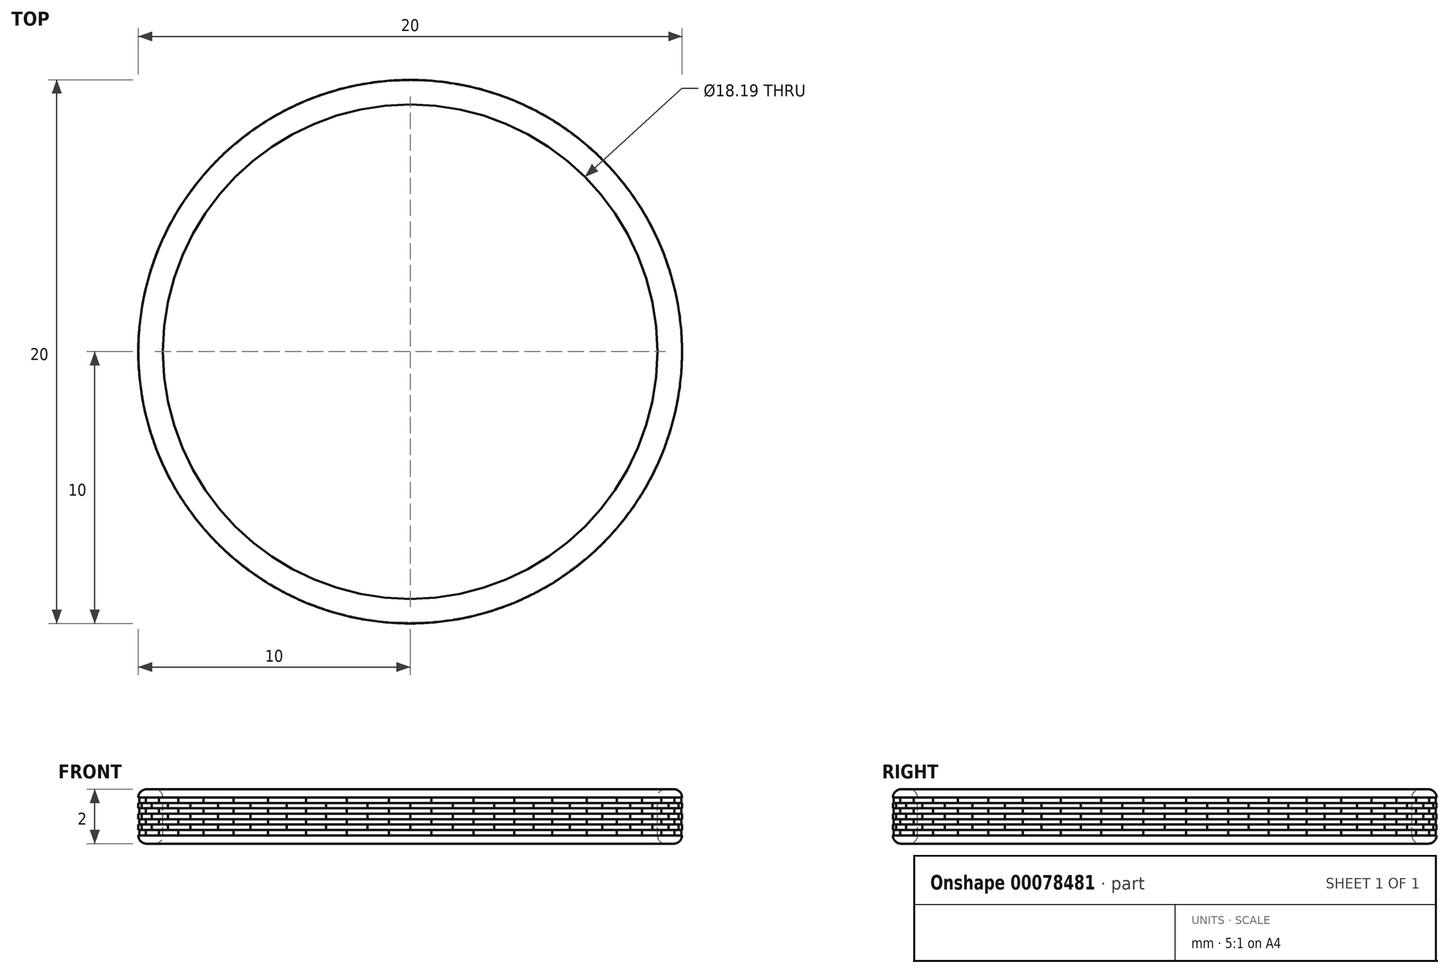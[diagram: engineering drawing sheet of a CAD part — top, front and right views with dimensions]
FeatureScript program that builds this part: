
annotation { "Feature Type Name" : "Feature", "Feature Type Description" : "" }
export const myFeature = defineFeature(function(context is Context, id is Id, definition is map)
    precondition{}
    {
        {
            var Q0;
            Q0=qCreatedBy(makeId("Top.planeOp"),FACE);
            var sketch = newSketch(context, id + "F0", { "sketchPlane" : qUnion([Q0])});
            skCircle(sketch, "E0", {"center": v(0, 0) * mm, "radius": 9.1 * mm});
            skLineSegment(sketch, "E1", {"start": v(0, 0) * mm, "end": v(-9.1, 0) * mm, "construction": true});
            skSolve(sketch);
        }
        {
            var Q0;
            Q0=qCreatedBy(makeId("Top.planeOp"),FACE);
            var sketch = newSketch(context, id + "F1", { "sketchPlane" : qUnion([Q0])});
            skCircle(sketch, "E2.cCircle", {"center": v(0, 0) * mm, "radius": 10 * mm, "construction": true});
            skLineSegment(sketch, "E2.0", {"start": v(10, 0) * mm, "end": v(9.88, -1.56) * mm});
            skLineSegment(sketch, "E2.1", {"start": v(9.88, -1.56) * mm, "end": v(9.51, -3.1) * mm});
            skLineSegment(sketch, "E2.2", {"start": v(9.51, -3.1) * mm, "end": v(8.91, -4.54) * mm});
            skLineSegment(sketch, "E2.3", {"start": v(8.91, -4.54) * mm, "end": v(8.1, -5.88) * mm});
            skLineSegment(sketch, "E2.4", {"start": v(8.1, -5.88) * mm, "end": v(7.07, -7.07) * mm});
            skLineSegment(sketch, "E2.5", {"start": v(7.07, -7.07) * mm, "end": v(5.88, -8.1) * mm});
            skLineSegment(sketch, "E2.6", {"start": v(5.88, -8.1) * mm, "end": v(4.54, -8.91) * mm});
            skLineSegment(sketch, "E2.7", {"start": v(4.54, -8.91) * mm, "end": v(3.1, -9.51) * mm});
            skLineSegment(sketch, "E2.8", {"start": v(3.1, -9.51) * mm, "end": v(1.56, -9.88) * mm});
            skLineSegment(sketch, "E2.9", {"start": v(1.56, -9.88) * mm, "end": v(0, -10) * mm});
            skLineSegment(sketch, "E2.10", {"start": v(0, -10) * mm, "end": v(-1.56, -9.88) * mm});
            skLineSegment(sketch, "E2.11", {"start": v(-1.56, -9.88) * mm, "end": v(-3.1, -9.51) * mm});
            skLineSegment(sketch, "E2.12", {"start": v(-3.1, -9.51) * mm, "end": v(-4.54, -8.91) * mm});
            skLineSegment(sketch, "E2.13", {"start": v(-4.54, -8.91) * mm, "end": v(-5.88, -8.1) * mm});
            skLineSegment(sketch, "E2.14", {"start": v(-5.88, -8.1) * mm, "end": v(-7.07, -7.07) * mm});
            skLineSegment(sketch, "E2.15", {"start": v(-7.07, -7.07) * mm, "end": v(-8.1, -5.88) * mm});
            skLineSegment(sketch, "E2.16", {"start": v(-8.1, -5.88) * mm, "end": v(-8.91, -4.54) * mm});
            skLineSegment(sketch, "E2.17", {"start": v(-8.91, -4.54) * mm, "end": v(-9.51, -3.1) * mm});
            skLineSegment(sketch, "E2.18", {"start": v(-9.51, -3.1) * mm, "end": v(-9.88, -1.56) * mm});
            skLineSegment(sketch, "E2.19", {"start": v(-9.88, -1.56) * mm, "end": v(-10, 0) * mm});
            skLineSegment(sketch, "E2.20", {"start": v(-10, 0) * mm, "end": v(-9.88, 1.56) * mm});
            skLineSegment(sketch, "E2.21", {"start": v(-9.88, 1.56) * mm, "end": v(-9.51, 3.1) * mm});
            skLineSegment(sketch, "E2.22", {"start": v(-9.51, 3.1) * mm, "end": v(-8.91, 4.54) * mm});
            skLineSegment(sketch, "E2.23", {"start": v(-8.91, 4.54) * mm, "end": v(-8.1, 5.88) * mm});
            skLineSegment(sketch, "E2.24", {"start": v(-8.1, 5.88) * mm, "end": v(-7.07, 7.07) * mm});
            skLineSegment(sketch, "E2.25", {"start": v(-7.07, 7.07) * mm, "end": v(-5.88, 8.1) * mm});
            skLineSegment(sketch, "E2.26", {"start": v(-5.88, 8.1) * mm, "end": v(-4.54, 8.91) * mm});
            skLineSegment(sketch, "E2.27", {"start": v(-4.54, 8.91) * mm, "end": v(-3.1, 9.51) * mm});
            skLineSegment(sketch, "E2.28", {"start": v(-3.1, 9.51) * mm, "end": v(-1.56, 9.88) * mm});
            skLineSegment(sketch, "E2.29", {"start": v(-1.56, 9.88) * mm, "end": v(0, 10) * mm});
            skLineSegment(sketch, "E2.30", {"start": v(0, 10) * mm, "end": v(1.56, 9.88) * mm});
            skLineSegment(sketch, "E2.31", {"start": v(1.56, 9.88) * mm, "end": v(3.1, 9.51) * mm});
            skLineSegment(sketch, "E2.32", {"start": v(3.1, 9.51) * mm, "end": v(4.54, 8.91) * mm});
            skLineSegment(sketch, "E2.33", {"start": v(4.54, 8.91) * mm, "end": v(5.88, 8.1) * mm});
            skLineSegment(sketch, "E2.34", {"start": v(5.88, 8.1) * mm, "end": v(7.07, 7.07) * mm});
            skLineSegment(sketch, "E2.35", {"start": v(7.07, 7.07) * mm, "end": v(8.1, 5.88) * mm});
            skLineSegment(sketch, "E2.36", {"start": v(8.1, 5.88) * mm, "end": v(8.91, 4.54) * mm});
            skLineSegment(sketch, "E2.37", {"start": v(8.91, 4.54) * mm, "end": v(9.51, 3.1) * mm});
            skLineSegment(sketch, "E2.38", {"start": v(9.51, 3.1) * mm, "end": v(9.88, 1.56) * mm});
            skLineSegment(sketch, "E2.39", {"start": v(9.88, 1.56) * mm, "end": v(10, 0) * mm});
            skLineSegment(sketch, "E3", {"start": v(0, 0) * mm, "end": v(-10, 0) * mm});
            skSolve(sketch);
        }
        {
            var Q0;
            Q0 = qSketchRegion(id + "F1", true);
            extrude(context, id + "F2", {"entities" : qUnion([Q0]), "endBound" : BoundingType.SYMMETRIC, "depth" : .2 * mm});
        }
        {
            var Q0;
            Q0=makeQuery(id+"F2.opExtrude","CAP_FACE",FACE,{"disambiguationData":[OSD([sQuery(id+"F1.wireOp",EDGE,"E2.0"),sQuery(id+"F1.wireOp",EDGE,"E2.1"),sQuery(id+"F1.wireOp",EDGE,"E2.2"),sQuery(id+"F1.wireOp",EDGE,"E2.3"),sQuery(id+"F1.wireOp",EDGE,"E2.4"),sQuery(id+"F1.wireOp",EDGE,"E2.5"),sQuery(id+"F1.wireOp",EDGE,"E2.6"),sQuery(id+"F1.wireOp",EDGE,"E2.7"),sQuery(id+"F1.wireOp",EDGE,"E2.8"),sQuery(id+"F1.wireOp",EDGE,"E2.9"),sQuery(id+"F1.wireOp",EDGE,"E2.10"),sQuery(id+"F1.wireOp",EDGE,"E2.11"),sQuery(id+"F1.wireOp",EDGE,"E2.12"),sQuery(id+"F1.wireOp",EDGE,"E2.13"),sQuery(id+"F1.wireOp",EDGE,"E2.14"),sQuery(id+"F1.wireOp",EDGE,"E2.15"),sQuery(id+"F1.wireOp",EDGE,"E2.16"),sQuery(id+"F1.wireOp",EDGE,"E2.17"),sQuery(id+"F1.wireOp",EDGE,"E2.18"),sQuery(id+"F1.wireOp",EDGE,"E2.19"),sQuery(id+"F1.wireOp",EDGE,"E2.20"),sQuery(id+"F1.wireOp",EDGE,"E2.21"),sQuery(id+"F1.wireOp",EDGE,"E2.22"),sQuery(id+"F1.wireOp",EDGE,"E2.23"),sQuery(id+"F1.wireOp",EDGE,"E2.24"),sQuery(id+"F1.wireOp",EDGE,"E2.25"),sQuery(id+"F1.wireOp",EDGE,"E2.26"),sQuery(id+"F1.wireOp",EDGE,"E2.27"),sQuery(id+"F1.wireOp",EDGE,"E2.28"),sQuery(id+"F1.wireOp",EDGE,"E2.29"),sQuery(id+"F1.wireOp",EDGE,"E2.30"),sQuery(id+"F1.wireOp",EDGE,"E2.31"),sQuery(id+"F1.wireOp",EDGE,"E2.32"),sQuery(id+"F1.wireOp",EDGE,"E2.33"),sQuery(id+"F1.wireOp",EDGE,"E2.34"),sQuery(id+"F1.wireOp",EDGE,"E2.35"),sQuery(id+"F1.wireOp",EDGE,"E2.36"),sQuery(id+"F1.wireOp",EDGE,"E2.37"),sQuery(id+"F1.wireOp",EDGE,"E2.38"),sQuery(id+"F1.wireOp",EDGE,"E2.39")])],"isStart":false});
            var sketch = newSketch(context, id + "F3", { "sketchPlane" : qUnion([Q0])});
            skCircle(sketch, "E4.cCircle", {"center": v(0, 0) * mm, "radius": 10 * mm, "construction": true});
            skLineSegment(sketch, "E4.0", {"start": v(9.24, 3.83) * mm, "end": v(9.72, 2.33) * mm});
            skLineSegment(sketch, "E4.1", {"start": v(9.72, 2.33) * mm, "end": v(9.97, 0.78) * mm});
            skLineSegment(sketch, "E4.2", {"start": v(9.97, 0.78) * mm, "end": v(9.97, -0.78) * mm});
            skLineSegment(sketch, "E4.3", {"start": v(9.97, -0.78) * mm, "end": v(9.72, -2.33) * mm});
            skLineSegment(sketch, "E4.4", {"start": v(9.72, -2.33) * mm, "end": v(9.24, -3.83) * mm});
            skLineSegment(sketch, "E4.5", {"start": v(9.24, -3.83) * mm, "end": v(8.53, -5.22) * mm});
            skLineSegment(sketch, "E4.6", {"start": v(8.53, -5.22) * mm, "end": v(7.6, -6.5) * mm});
            skLineSegment(sketch, "E4.7", {"start": v(7.6, -6.5) * mm, "end": v(6.5, -7.6) * mm});
            skLineSegment(sketch, "E4.8", {"start": v(6.5, -7.6) * mm, "end": v(5.22, -8.53) * mm});
            skLineSegment(sketch, "E4.9", {"start": v(5.22, -8.53) * mm, "end": v(3.83, -9.24) * mm});
            skLineSegment(sketch, "E4.10", {"start": v(3.83, -9.24) * mm, "end": v(2.33, -9.72) * mm});
            skLineSegment(sketch, "E4.11", {"start": v(2.33, -9.72) * mm, "end": v(0.78, -9.97) * mm});
            skLineSegment(sketch, "E4.12", {"start": v(0.78, -9.97) * mm, "end": v(-0.78, -9.97) * mm});
            skLineSegment(sketch, "E4.13", {"start": v(-0.78, -9.97) * mm, "end": v(-2.33, -9.72) * mm});
            skLineSegment(sketch, "E4.14", {"start": v(-2.33, -9.72) * mm, "end": v(-3.83, -9.24) * mm});
            skLineSegment(sketch, "E4.15", {"start": v(-3.83, -9.24) * mm, "end": v(-5.22, -8.53) * mm});
            skLineSegment(sketch, "E4.16", {"start": v(-5.22, -8.53) * mm, "end": v(-6.5, -7.6) * mm});
            skLineSegment(sketch, "E4.17", {"start": v(-6.5, -7.6) * mm, "end": v(-7.6, -6.5) * mm});
            skLineSegment(sketch, "E4.18", {"start": v(-7.6, -6.5) * mm, "end": v(-8.53, -5.22) * mm});
            skLineSegment(sketch, "E4.19", {"start": v(-8.53, -5.22) * mm, "end": v(-9.24, -3.83) * mm});
            skLineSegment(sketch, "E4.20", {"start": v(-9.24, -3.83) * mm, "end": v(-9.72, -2.33) * mm});
            skLineSegment(sketch, "E4.21", {"start": v(-9.72, -2.33) * mm, "end": v(-9.97, -0.78) * mm});
            skLineSegment(sketch, "E4.22", {"start": v(-9.97, -0.78) * mm, "end": v(-9.97, 0.78) * mm});
            skLineSegment(sketch, "E4.23", {"start": v(-9.97, 0.78) * mm, "end": v(-9.72, 2.33) * mm});
            skLineSegment(sketch, "E4.24", {"start": v(-9.72, 2.33) * mm, "end": v(-9.24, 3.83) * mm});
            skLineSegment(sketch, "E4.25", {"start": v(-9.24, 3.83) * mm, "end": v(-8.53, 5.22) * mm});
            skLineSegment(sketch, "E4.26", {"start": v(-8.53, 5.22) * mm, "end": v(-7.6, 6.5) * mm});
            skLineSegment(sketch, "E4.27", {"start": v(-7.6, 6.5) * mm, "end": v(-6.5, 7.6) * mm});
            skLineSegment(sketch, "E4.28", {"start": v(-6.5, 7.6) * mm, "end": v(-5.22, 8.53) * mm});
            skLineSegment(sketch, "E4.29", {"start": v(-5.22, 8.53) * mm, "end": v(-3.83, 9.24) * mm});
            skLineSegment(sketch, "E4.30", {"start": v(-3.83, 9.24) * mm, "end": v(-2.33, 9.72) * mm});
            skLineSegment(sketch, "E4.31", {"start": v(-2.33, 9.72) * mm, "end": v(-0.78, 9.97) * mm});
            skLineSegment(sketch, "E4.32", {"start": v(-0.78, 9.97) * mm, "end": v(0.78, 9.97) * mm});
            skLineSegment(sketch, "E4.33", {"start": v(0.78, 9.97) * mm, "end": v(2.33, 9.72) * mm});
            skLineSegment(sketch, "E4.34", {"start": v(2.33, 9.72) * mm, "end": v(3.83, 9.24) * mm});
            skLineSegment(sketch, "E4.35", {"start": v(3.83, 9.24) * mm, "end": v(5.22, 8.53) * mm});
            skLineSegment(sketch, "E4.36", {"start": v(5.22, 8.53) * mm, "end": v(6.5, 7.6) * mm});
            skLineSegment(sketch, "E4.37", {"start": v(6.5, 7.6) * mm, "end": v(7.6, 6.5) * mm});
            skLineSegment(sketch, "E4.38", {"start": v(7.6, 6.5) * mm, "end": v(8.53, 5.22) * mm});
            skLineSegment(sketch, "E4.39", {"start": v(8.53, 5.22) * mm, "end": v(9.24, 3.83) * mm});
            skLineSegment(sketch, "E5", {"start": v(0, 0) * mm, "end": v(-9.97, 0.78) * mm});
            skSolve(sketch);
        }
        {
            var Q0;
            Q0 = qSketchRegion(id + "F3", true);
            extrude(context, id + "F4", {"entities" : qUnion([Q0]), "depth" : .2 * mm});
        }
        {
            var Q0;
            Q0=makeQuery(id+"F4.opExtrude","CAP_FACE",FACE,{"disambiguationData":[OSD([sQuery(id+"F3.wireOp",EDGE,"E4.0"),sQuery(id+"F3.wireOp",EDGE,"E4.1"),sQuery(id+"F3.wireOp",EDGE,"E4.2"),sQuery(id+"F3.wireOp",EDGE,"E4.3"),sQuery(id+"F3.wireOp",EDGE,"E4.4"),sQuery(id+"F3.wireOp",EDGE,"E4.5"),sQuery(id+"F3.wireOp",EDGE,"E4.6"),sQuery(id+"F3.wireOp",EDGE,"E4.7"),sQuery(id+"F3.wireOp",EDGE,"E4.8"),sQuery(id+"F3.wireOp",EDGE,"E4.9"),sQuery(id+"F3.wireOp",EDGE,"E4.10"),sQuery(id+"F3.wireOp",EDGE,"E4.11"),sQuery(id+"F3.wireOp",EDGE,"E4.12"),sQuery(id+"F3.wireOp",EDGE,"E4.13"),sQuery(id+"F3.wireOp",EDGE,"E4.14"),sQuery(id+"F3.wireOp",EDGE,"E4.15"),sQuery(id+"F3.wireOp",EDGE,"E4.16"),sQuery(id+"F3.wireOp",EDGE,"E4.17"),sQuery(id+"F3.wireOp",EDGE,"E4.18"),sQuery(id+"F3.wireOp",EDGE,"E4.19"),sQuery(id+"F3.wireOp",EDGE,"E4.20"),sQuery(id+"F3.wireOp",EDGE,"E4.21"),sQuery(id+"F3.wireOp",EDGE,"E4.22"),sQuery(id+"F3.wireOp",EDGE,"E4.23"),sQuery(id+"F3.wireOp",EDGE,"E4.24"),sQuery(id+"F3.wireOp",EDGE,"E4.25"),sQuery(id+"F3.wireOp",EDGE,"E4.26"),sQuery(id+"F3.wireOp",EDGE,"E4.27"),sQuery(id+"F3.wireOp",EDGE,"E4.28"),sQuery(id+"F3.wireOp",EDGE,"E4.29"),sQuery(id+"F3.wireOp",EDGE,"E4.30"),sQuery(id+"F3.wireOp",EDGE,"E4.31"),sQuery(id+"F3.wireOp",EDGE,"E4.32"),sQuery(id+"F3.wireOp",EDGE,"E4.33"),sQuery(id+"F3.wireOp",EDGE,"E4.34"),sQuery(id+"F3.wireOp",EDGE,"E4.35"),sQuery(id+"F3.wireOp",EDGE,"E4.36"),sQuery(id+"F3.wireOp",EDGE,"E4.37"),sQuery(id+"F3.wireOp",EDGE,"E4.38"),sQuery(id+"F3.wireOp",EDGE,"E4.39")])],"isStart":false});
            var sketch = newSketch(context, id + "F5", { "sketchPlane" : qUnion([Q0])});
            skCircle(sketch, "E6.cCircle", {"center": v(0, 0) * mm, "radius": 10 * mm, "construction": true});
            skLineSegment(sketch, "E6.0", {"start": v(10, 0) * mm, "end": v(9.88, -1.56) * mm});
            skLineSegment(sketch, "E6.1", {"start": v(9.88, -1.56) * mm, "end": v(9.51, -3.1) * mm});
            skLineSegment(sketch, "E6.2", {"start": v(9.51, -3.1) * mm, "end": v(8.91, -4.54) * mm});
            skLineSegment(sketch, "E6.3", {"start": v(8.91, -4.54) * mm, "end": v(8.1, -5.88) * mm});
            skLineSegment(sketch, "E6.4", {"start": v(8.1, -5.88) * mm, "end": v(7.07, -7.07) * mm});
            skLineSegment(sketch, "E6.5", {"start": v(7.07, -7.07) * mm, "end": v(5.88, -8.1) * mm});
            skLineSegment(sketch, "E6.6", {"start": v(5.88, -8.1) * mm, "end": v(4.54, -8.91) * mm});
            skLineSegment(sketch, "E6.7", {"start": v(4.54, -8.91) * mm, "end": v(3.1, -9.51) * mm});
            skLineSegment(sketch, "E6.8", {"start": v(3.1, -9.51) * mm, "end": v(1.56, -9.88) * mm});
            skLineSegment(sketch, "E6.9", {"start": v(1.56, -9.88) * mm, "end": v(0, -10) * mm});
            skLineSegment(sketch, "E6.10", {"start": v(0, -10) * mm, "end": v(-1.56, -9.88) * mm});
            skLineSegment(sketch, "E6.11", {"start": v(-1.56, -9.88) * mm, "end": v(-3.1, -9.51) * mm});
            skLineSegment(sketch, "E6.12", {"start": v(-3.1, -9.51) * mm, "end": v(-4.54, -8.91) * mm});
            skLineSegment(sketch, "E6.13", {"start": v(-4.54, -8.91) * mm, "end": v(-5.88, -8.1) * mm});
            skLineSegment(sketch, "E6.14", {"start": v(-5.88, -8.1) * mm, "end": v(-7.07, -7.07) * mm});
            skLineSegment(sketch, "E6.15", {"start": v(-7.07, -7.07) * mm, "end": v(-8.1, -5.88) * mm});
            skLineSegment(sketch, "E6.16", {"start": v(-8.1, -5.88) * mm, "end": v(-8.91, -4.54) * mm});
            skLineSegment(sketch, "E6.17", {"start": v(-8.91, -4.54) * mm, "end": v(-9.51, -3.1) * mm});
            skLineSegment(sketch, "E6.18", {"start": v(-9.51, -3.1) * mm, "end": v(-9.88, -1.56) * mm});
            skLineSegment(sketch, "E6.19", {"start": v(-9.88, -1.56) * mm, "end": v(-10, 0) * mm});
            skLineSegment(sketch, "E6.20", {"start": v(-10, 0) * mm, "end": v(-9.88, 1.56) * mm});
            skLineSegment(sketch, "E6.21", {"start": v(-9.88, 1.56) * mm, "end": v(-9.51, 3.1) * mm});
            skLineSegment(sketch, "E6.22", {"start": v(-9.51, 3.1) * mm, "end": v(-8.91, 4.54) * mm});
            skLineSegment(sketch, "E6.23", {"start": v(-8.91, 4.54) * mm, "end": v(-8.1, 5.88) * mm});
            skLineSegment(sketch, "E6.24", {"start": v(-8.1, 5.88) * mm, "end": v(-7.07, 7.07) * mm});
            skLineSegment(sketch, "E6.25", {"start": v(-7.07, 7.07) * mm, "end": v(-5.88, 8.1) * mm});
            skLineSegment(sketch, "E6.26", {"start": v(-5.88, 8.1) * mm, "end": v(-4.54, 8.91) * mm});
            skLineSegment(sketch, "E6.27", {"start": v(-4.54, 8.91) * mm, "end": v(-3.1, 9.51) * mm});
            skLineSegment(sketch, "E6.28", {"start": v(-3.1, 9.51) * mm, "end": v(-1.56, 9.88) * mm});
            skLineSegment(sketch, "E6.29", {"start": v(-1.56, 9.88) * mm, "end": v(0, 10) * mm});
            skLineSegment(sketch, "E6.30", {"start": v(0, 10) * mm, "end": v(1.56, 9.88) * mm});
            skLineSegment(sketch, "E6.31", {"start": v(1.56, 9.88) * mm, "end": v(3.1, 9.51) * mm});
            skLineSegment(sketch, "E6.32", {"start": v(3.1, 9.51) * mm, "end": v(4.54, 8.91) * mm});
            skLineSegment(sketch, "E6.33", {"start": v(4.54, 8.91) * mm, "end": v(5.88, 8.1) * mm});
            skLineSegment(sketch, "E6.34", {"start": v(5.88, 8.1) * mm, "end": v(7.07, 7.07) * mm});
            skLineSegment(sketch, "E6.35", {"start": v(7.07, 7.07) * mm, "end": v(8.1, 5.88) * mm});
            skLineSegment(sketch, "E6.36", {"start": v(8.1, 5.88) * mm, "end": v(8.91, 4.54) * mm});
            skLineSegment(sketch, "E6.37", {"start": v(8.91, 4.54) * mm, "end": v(9.51, 3.1) * mm});
            skLineSegment(sketch, "E6.38", {"start": v(9.51, 3.1) * mm, "end": v(9.88, 1.56) * mm});
            skLineSegment(sketch, "E6.39", {"start": v(9.88, 1.56) * mm, "end": v(10, 0) * mm});
            skLineSegment(sketch, "E7", {"start": v(0, 0) * mm, "end": v(-10, 0) * mm, "construction": true});
            skSolve(sketch);
        }
        {
            var Q0;
            Q0 = qSketchRegion(id + "F5", true);
            extrude(context, id + "F6", {"entities" : qUnion([Q0]), "operationType" : NewBodyOperationType.ADD, "depth" : .2 * mm});
        }
        {
            var Q0;
            Q0=makeQuery(id+"F6.opExtrude","CAP_FACE",FACE,{"disambiguationData":[OSD([sQuery(id+"F5.wireOp",EDGE,"E6.0"),sQuery(id+"F5.wireOp",EDGE,"E6.1"),sQuery(id+"F5.wireOp",EDGE,"E6.2"),sQuery(id+"F5.wireOp",EDGE,"E6.3"),sQuery(id+"F5.wireOp",EDGE,"E6.4"),sQuery(id+"F5.wireOp",EDGE,"E6.5"),sQuery(id+"F5.wireOp",EDGE,"E6.6"),sQuery(id+"F5.wireOp",EDGE,"E6.7"),sQuery(id+"F5.wireOp",EDGE,"E6.8"),sQuery(id+"F5.wireOp",EDGE,"E6.9"),sQuery(id+"F5.wireOp",EDGE,"E6.10"),sQuery(id+"F5.wireOp",EDGE,"E6.11"),sQuery(id+"F5.wireOp",EDGE,"E6.12"),sQuery(id+"F5.wireOp",EDGE,"E6.13"),sQuery(id+"F5.wireOp",EDGE,"E6.14"),sQuery(id+"F5.wireOp",EDGE,"E6.15"),sQuery(id+"F5.wireOp",EDGE,"E6.16"),sQuery(id+"F5.wireOp",EDGE,"E6.17"),sQuery(id+"F5.wireOp",EDGE,"E6.18"),sQuery(id+"F5.wireOp",EDGE,"E6.19"),sQuery(id+"F5.wireOp",EDGE,"E6.20"),sQuery(id+"F5.wireOp",EDGE,"E6.21"),sQuery(id+"F5.wireOp",EDGE,"E6.22"),sQuery(id+"F5.wireOp",EDGE,"E6.23"),sQuery(id+"F5.wireOp",EDGE,"E6.24"),sQuery(id+"F5.wireOp",EDGE,"E6.25"),sQuery(id+"F5.wireOp",EDGE,"E6.26"),sQuery(id+"F5.wireOp",EDGE,"E6.27"),sQuery(id+"F5.wireOp",EDGE,"E6.28"),sQuery(id+"F5.wireOp",EDGE,"E6.29"),sQuery(id+"F5.wireOp",EDGE,"E6.30"),sQuery(id+"F5.wireOp",EDGE,"E6.31"),sQuery(id+"F5.wireOp",EDGE,"E6.32"),sQuery(id+"F5.wireOp",EDGE,"E6.33"),sQuery(id+"F5.wireOp",EDGE,"E6.34"),sQuery(id+"F5.wireOp",EDGE,"E6.35"),sQuery(id+"F5.wireOp",EDGE,"E6.36"),sQuery(id+"F5.wireOp",EDGE,"E6.37"),sQuery(id+"F5.wireOp",EDGE,"E6.38"),sQuery(id+"F5.wireOp",EDGE,"E6.39")])],"isStart":false});
            var sketch = newSketch(context, id + "F7", { "sketchPlane" : qUnion([Q0])});
            skCircle(sketch, "E8.cCircle", {"center": v(0, 0) * mm, "radius": 10 * mm, "construction": true});
            skLineSegment(sketch, "E8.0", {"start": v(9.24, 3.83) * mm, "end": v(9.72, 2.33) * mm});
            skLineSegment(sketch, "E8.1", {"start": v(9.72, 2.33) * mm, "end": v(9.97, 0.78) * mm});
            skLineSegment(sketch, "E8.2", {"start": v(9.97, 0.78) * mm, "end": v(9.97, -0.78) * mm});
            skLineSegment(sketch, "E8.3", {"start": v(9.97, -0.78) * mm, "end": v(9.72, -2.33) * mm});
            skLineSegment(sketch, "E8.4", {"start": v(9.72, -2.33) * mm, "end": v(9.24, -3.83) * mm});
            skLineSegment(sketch, "E8.5", {"start": v(9.24, -3.83) * mm, "end": v(8.53, -5.22) * mm});
            skLineSegment(sketch, "E8.6", {"start": v(8.53, -5.22) * mm, "end": v(7.6, -6.5) * mm});
            skLineSegment(sketch, "E8.7", {"start": v(7.6, -6.5) * mm, "end": v(6.5, -7.6) * mm});
            skLineSegment(sketch, "E8.8", {"start": v(6.5, -7.6) * mm, "end": v(5.22, -8.53) * mm});
            skLineSegment(sketch, "E8.9", {"start": v(5.22, -8.53) * mm, "end": v(3.83, -9.24) * mm});
            skLineSegment(sketch, "E8.10", {"start": v(3.83, -9.24) * mm, "end": v(2.33, -9.72) * mm});
            skLineSegment(sketch, "E8.11", {"start": v(2.33, -9.72) * mm, "end": v(0.78, -9.97) * mm});
            skLineSegment(sketch, "E8.12", {"start": v(0.78, -9.97) * mm, "end": v(-0.78, -9.97) * mm});
            skLineSegment(sketch, "E8.13", {"start": v(-0.78, -9.97) * mm, "end": v(-2.33, -9.72) * mm});
            skLineSegment(sketch, "E8.14", {"start": v(-2.33, -9.72) * mm, "end": v(-3.83, -9.24) * mm});
            skLineSegment(sketch, "E8.15", {"start": v(-3.83, -9.24) * mm, "end": v(-5.22, -8.53) * mm});
            skLineSegment(sketch, "E8.16", {"start": v(-5.22, -8.53) * mm, "end": v(-6.5, -7.6) * mm});
            skLineSegment(sketch, "E8.17", {"start": v(-6.5, -7.6) * mm, "end": v(-7.6, -6.5) * mm});
            skLineSegment(sketch, "E8.18", {"start": v(-7.6, -6.5) * mm, "end": v(-8.53, -5.22) * mm});
            skLineSegment(sketch, "E8.19", {"start": v(-8.53, -5.22) * mm, "end": v(-9.24, -3.83) * mm});
            skLineSegment(sketch, "E8.20", {"start": v(-9.24, -3.83) * mm, "end": v(-9.72, -2.33) * mm});
            skLineSegment(sketch, "E8.21", {"start": v(-9.72, -2.33) * mm, "end": v(-9.97, -0.78) * mm});
            skLineSegment(sketch, "E8.22", {"start": v(-9.97, -0.78) * mm, "end": v(-9.97, 0.78) * mm});
            skLineSegment(sketch, "E8.23", {"start": v(-9.97, 0.78) * mm, "end": v(-9.72, 2.33) * mm});
            skLineSegment(sketch, "E8.24", {"start": v(-9.72, 2.33) * mm, "end": v(-9.24, 3.83) * mm});
            skLineSegment(sketch, "E8.25", {"start": v(-9.24, 3.83) * mm, "end": v(-8.53, 5.22) * mm});
            skLineSegment(sketch, "E8.26", {"start": v(-8.53, 5.22) * mm, "end": v(-7.6, 6.5) * mm});
            skLineSegment(sketch, "E8.27", {"start": v(-7.6, 6.5) * mm, "end": v(-6.5, 7.6) * mm});
            skLineSegment(sketch, "E8.28", {"start": v(-6.5, 7.6) * mm, "end": v(-5.22, 8.53) * mm});
            skLineSegment(sketch, "E8.29", {"start": v(-5.22, 8.53) * mm, "end": v(-3.83, 9.24) * mm});
            skLineSegment(sketch, "E8.30", {"start": v(-3.83, 9.24) * mm, "end": v(-2.33, 9.72) * mm});
            skLineSegment(sketch, "E8.31", {"start": v(-2.33, 9.72) * mm, "end": v(-0.78, 9.97) * mm});
            skLineSegment(sketch, "E8.32", {"start": v(-0.78, 9.97) * mm, "end": v(0.78, 9.97) * mm});
            skLineSegment(sketch, "E8.33", {"start": v(0.78, 9.97) * mm, "end": v(2.33, 9.72) * mm});
            skLineSegment(sketch, "E8.34", {"start": v(2.33, 9.72) * mm, "end": v(3.83, 9.24) * mm});
            skLineSegment(sketch, "E8.35", {"start": v(3.83, 9.24) * mm, "end": v(5.22, 8.53) * mm});
            skLineSegment(sketch, "E8.36", {"start": v(5.22, 8.53) * mm, "end": v(6.5, 7.6) * mm});
            skLineSegment(sketch, "E8.37", {"start": v(6.5, 7.6) * mm, "end": v(7.6, 6.5) * mm});
            skLineSegment(sketch, "E8.38", {"start": v(7.6, 6.5) * mm, "end": v(8.53, 5.22) * mm});
            skLineSegment(sketch, "E8.39", {"start": v(8.53, 5.22) * mm, "end": v(9.24, 3.83) * mm});
            skLineSegment(sketch, "E9", {"start": v(0, 0) * mm, "end": v(-9.97, 0.78) * mm, "construction": true});
            skSolve(sketch);
        }
        {
            var Q0;
            Q0 = qSketchRegion(id + "F7", true);
            extrude(context, id + "F8", {"entities" : qUnion([Q0]), "operationType" : NewBodyOperationType.ADD, "depth" : .2 * mm});
        }
        {
            var Q0;
            Q0=makeQuery(id+"F8.opExtrude","CAP_FACE",FACE,{"disambiguationData":[OSD([sQuery(id+"F7.wireOp",EDGE,"E8.0"),sQuery(id+"F7.wireOp",EDGE,"E8.1"),sQuery(id+"F7.wireOp",EDGE,"E8.2"),sQuery(id+"F7.wireOp",EDGE,"E8.3"),sQuery(id+"F7.wireOp",EDGE,"E8.4"),sQuery(id+"F7.wireOp",EDGE,"E8.5"),sQuery(id+"F7.wireOp",EDGE,"E8.6"),sQuery(id+"F7.wireOp",EDGE,"E8.7"),sQuery(id+"F7.wireOp",EDGE,"E8.8"),sQuery(id+"F7.wireOp",EDGE,"E8.9"),sQuery(id+"F7.wireOp",EDGE,"E8.10"),sQuery(id+"F7.wireOp",EDGE,"E8.11"),sQuery(id+"F7.wireOp",EDGE,"E8.12"),sQuery(id+"F7.wireOp",EDGE,"E8.13"),sQuery(id+"F7.wireOp",EDGE,"E8.14"),sQuery(id+"F7.wireOp",EDGE,"E8.15"),sQuery(id+"F7.wireOp",EDGE,"E8.16"),sQuery(id+"F7.wireOp",EDGE,"E8.17"),sQuery(id+"F7.wireOp",EDGE,"E8.18"),sQuery(id+"F7.wireOp",EDGE,"E8.19"),sQuery(id+"F7.wireOp",EDGE,"E8.20"),sQuery(id+"F7.wireOp",EDGE,"E8.21"),sQuery(id+"F7.wireOp",EDGE,"E8.22"),sQuery(id+"F7.wireOp",EDGE,"E8.23"),sQuery(id+"F7.wireOp",EDGE,"E8.24"),sQuery(id+"F7.wireOp",EDGE,"E8.25"),sQuery(id+"F7.wireOp",EDGE,"E8.26"),sQuery(id+"F7.wireOp",EDGE,"E8.27"),sQuery(id+"F7.wireOp",EDGE,"E8.28"),sQuery(id+"F7.wireOp",EDGE,"E8.29"),sQuery(id+"F7.wireOp",EDGE,"E8.30"),sQuery(id+"F7.wireOp",EDGE,"E8.31"),sQuery(id+"F7.wireOp",EDGE,"E8.32"),sQuery(id+"F7.wireOp",EDGE,"E8.33"),sQuery(id+"F7.wireOp",EDGE,"E8.34"),sQuery(id+"F7.wireOp",EDGE,"E8.35"),sQuery(id+"F7.wireOp",EDGE,"E8.36"),sQuery(id+"F7.wireOp",EDGE,"E8.37"),sQuery(id+"F7.wireOp",EDGE,"E8.38"),sQuery(id+"F7.wireOp",EDGE,"E8.39")])],"isStart":false});
            var sketch = newSketch(context, id + "F9", { "sketchPlane" : qUnion([Q0])});
            skCircle(sketch, "E10", {"center": v(0, 0) * mm, "radius": 10 * mm});
            skSolve(sketch);
        }
        {
            var Q0;
            Q0 = qSketchRegion(id + "F9", true);
            extrude(context, id + "F10", {"entities" : qUnion([Q0]), "operationType" : NewBodyOperationType.ADD, "depth" : .3 * mm});
        }
        {
            var Q0;
            Q0=makeQuery(id+"F4.opExtrude","SWEPT_BODY",BODY,{"disambiguationData":[OSD([sQuery(id+"F3.wireOp",EDGE,"E4.0"),sQuery(id+"F3.wireOp",EDGE,"E4.1"),sQuery(id+"F3.wireOp",EDGE,"E4.2"),sQuery(id+"F3.wireOp",EDGE,"E4.3"),sQuery(id+"F3.wireOp",EDGE,"E4.4"),sQuery(id+"F3.wireOp",EDGE,"E4.5"),sQuery(id+"F3.wireOp",EDGE,"E4.6"),sQuery(id+"F3.wireOp",EDGE,"E4.7"),sQuery(id+"F3.wireOp",EDGE,"E4.8"),sQuery(id+"F3.wireOp",EDGE,"E4.9"),sQuery(id+"F3.wireOp",EDGE,"E4.10"),sQuery(id+"F3.wireOp",EDGE,"E4.11"),sQuery(id+"F3.wireOp",EDGE,"E4.12"),sQuery(id+"F3.wireOp",EDGE,"E4.13"),sQuery(id+"F3.wireOp",EDGE,"E4.14"),sQuery(id+"F3.wireOp",EDGE,"E4.15"),sQuery(id+"F3.wireOp",EDGE,"E4.16"),sQuery(id+"F3.wireOp",EDGE,"E4.17"),sQuery(id+"F3.wireOp",EDGE,"E4.18"),sQuery(id+"F3.wireOp",EDGE,"E4.19"),sQuery(id+"F3.wireOp",EDGE,"E4.20"),sQuery(id+"F3.wireOp",EDGE,"E4.21"),sQuery(id+"F3.wireOp",EDGE,"E4.22"),sQuery(id+"F3.wireOp",EDGE,"E4.23"),sQuery(id+"F3.wireOp",EDGE,"E4.24"),sQuery(id+"F3.wireOp",EDGE,"E4.25"),sQuery(id+"F3.wireOp",EDGE,"E4.26"),sQuery(id+"F3.wireOp",EDGE,"E4.27"),sQuery(id+"F3.wireOp",EDGE,"E4.28"),sQuery(id+"F3.wireOp",EDGE,"E4.29"),sQuery(id+"F3.wireOp",EDGE,"E4.30"),sQuery(id+"F3.wireOp",EDGE,"E4.31"),sQuery(id+"F3.wireOp",EDGE,"E4.32"),sQuery(id+"F3.wireOp",EDGE,"E4.33"),sQuery(id+"F3.wireOp",EDGE,"E4.34"),sQuery(id+"F3.wireOp",EDGE,"E4.35"),sQuery(id+"F3.wireOp",EDGE,"E4.36"),sQuery(id+"F3.wireOp",EDGE,"E4.37"),sQuery(id+"F3.wireOp",EDGE,"E4.38"),sQuery(id+"F3.wireOp",EDGE,"E4.39")])]});
            var Q1;
            Q1=makeQuery(id+"F10.opExtrude","SWEPT_BODY",BODY,{"disambiguationData":[OSD([sQuery(id+"F9.wireOp",EDGE,"E10")])]});
            var Q2;
            Q2=qCreatedBy(makeId("Top.planeOp"),FACE);
            mirror(context, id + "F11", {"operationType" : NewBodyOperationType.ADD, "entities" : qUnion([Q0, Q1]), "mirrorPlane" : qUnion([Q2])});
        }
        {
            var Q0;
            Q0 = qSketchRegion(id + "F0", true);
            extrude(context, id + "F12", {"entities" : qUnion([Q0]), "operationType" : NewBodyOperationType.REMOVE, "endBound" : BoundingType.SYMMETRIC, "oppositeDirection" : true, "depth" : 10 * mm});
        }
        {
            var Q0;
            Q0=makeQuery(id+"F10.opExtrude","CAP_FACE",FACE,{"disambiguationData":[OSD([sQuery(id+"F9.wireOp",EDGE,"E10")])],"isStart":false});
            var Q1;
            Q1=makeQuery(id+"F11.opPattern","COPY",FACE,{"derivedFrom":makeQuery(id+"F10.opExtrude","CAP_FACE",FACE,{"disambiguationData":[OSD([sQuery(id+"F9.wireOp",EDGE,"E10")])],"isStart":false}),"instanceName":"1"});
            fillet(context, id + "F13", {"entities" : qUnion([Q0, Q1]), "radius" : .3 * mm, "tangentPropagation" : true, "allowEdgeOverflow" : false});
        }
    });
